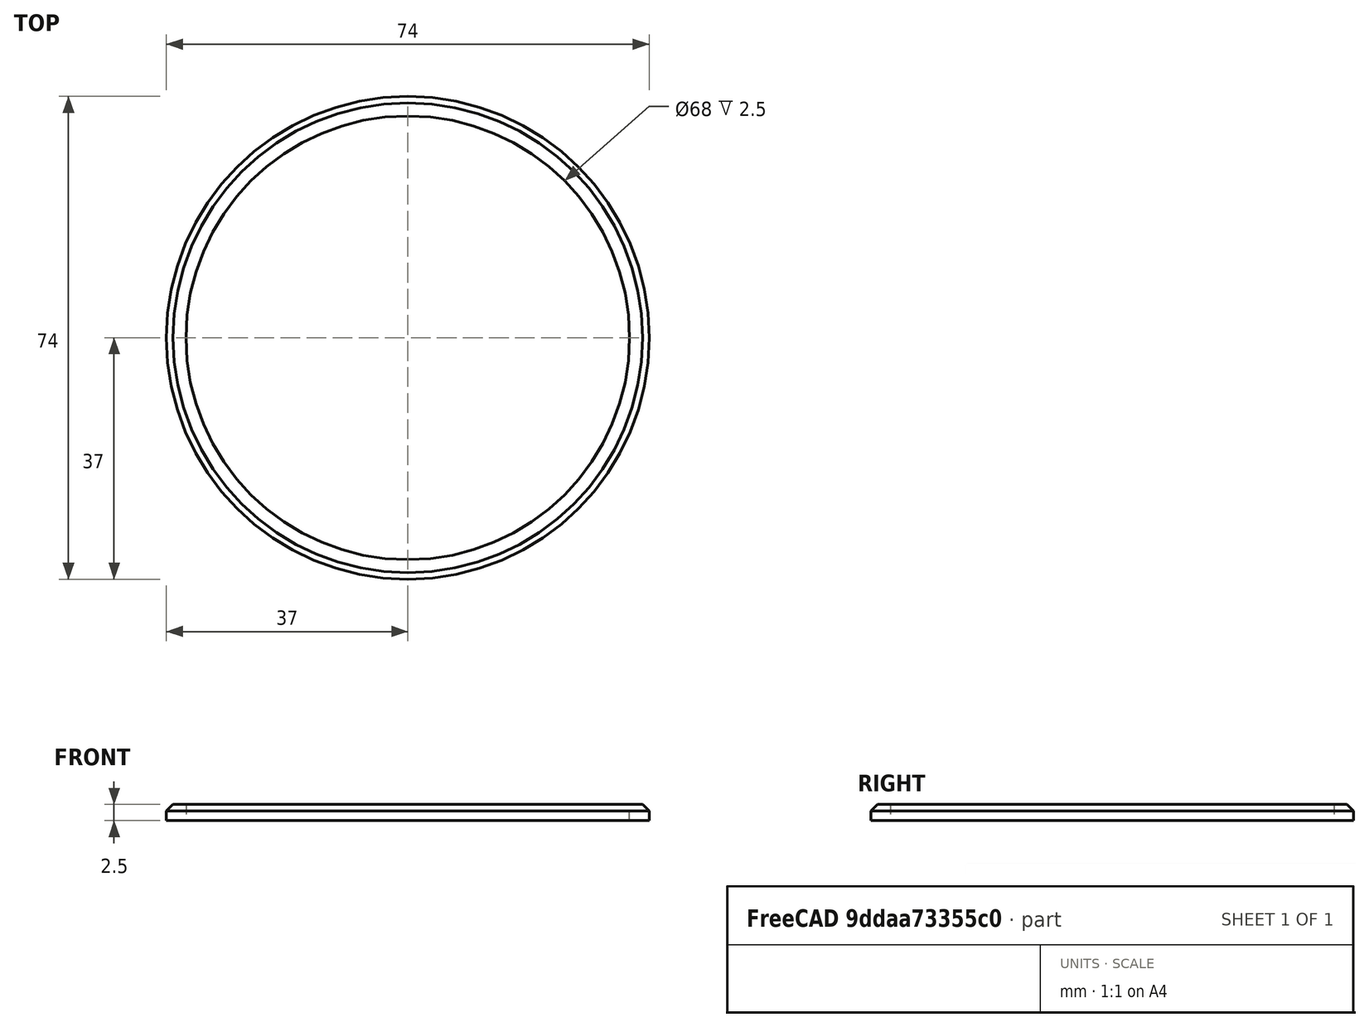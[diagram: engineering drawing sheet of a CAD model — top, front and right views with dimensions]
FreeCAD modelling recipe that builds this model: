
FCSTD DOCUMENT  (FreeCAD 0.19R24276 (Git))
Label: ring_68x74x2_5
License: All rights reserved
LicenseURL: http://en.wikipedia.org/wiki/All_rights_reserved
objects: Sketcher::SketchObject×1, PartDesign::Pad×1, PartDesign::Chamfer×1, PartDesign::Body×1
note: 6 computed .brp shape members not serialized (recipe doc carries the construction recipe); baked Part::Feature solids carry a one-line shape summary decoded from their .brp

FEATURE [Sketcher::SketchObject] Sketch
  FullyConstrained = true
  MapMode = 5
  Support = -> [XY_Plane]
  sketch-geometry (2):
    g0: Circle CenterX=0 CenterY=0 CenterZ=0 NormalX=0 NormalY=0 NormalZ=1 AngleXU=0 Radius=37
    g1: Circle CenterX=0 CenterY=0 CenterZ=0 NormalX=0 NormalY=0 NormalZ=1 AngleXU=0 Radius=34
  constraints (4):
    c: Coincident(g0,g-1)
    c: Coincident(g1,g0)
    c: Diameter(g1) = 68
    c: Diameter(g0) = 74
FEATURE [PartDesign::Pad] Pad
  Direction = (1,1,1)
  Length = 2.5
  Length2 = 100
  Profile = -> Sketch
  Type = 0
FEATURE [PartDesign::Chamfer] Chamfer
  Angle = 45
  Base = -> Pad [Edge3]
  BaseFeature = -> Pad
  ChamferType = 0
  FlipDirection = false
  Size = 1
  Size2 = 1
  SupportTransform = false
FEATURE [PartDesign::Body] Body
  Group = -> [Sketch,Pad,Chamfer]
  Origin = -> Origin
  Tip = -> Chamfer
